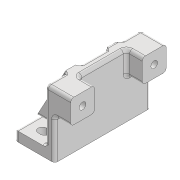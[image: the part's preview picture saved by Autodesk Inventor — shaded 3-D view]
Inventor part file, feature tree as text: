
AUTODESK INVENTOR PART (.ipt)
format: ipt  version: 2020 (Build 240168000, 168)  size: 386,048 bytes
history: native  units: mm
features: extrude x8, sketch x8, chamfer x2, other x1, fillet x1
ambient origin geometry x8: Origin, YZ Plane, XZ Plane, XY Plane, X Axis, Y Axis, Z Axis, Center Point
bodies: Body1 (feature_tree)
feature tree (20):
  other  "Sólido1"
  extrude  "Extrusão1"  Depth=40.0mm
  extrude  "Extrusão2"  Depth=6.0mm
  extrude  "Extrusão3"  Depth=6.0mm TaperAngle=0.0deg
  extrude  "Extrusão4"  TaperAngle=0.0deg  [1 undecoded]
  extrude  "Extrusão5"  Depth=15.0mm
  extrude  "Extrusão6"  Depth=4.2mm
  extrude  "Extrusão7"  Depth=10.0mm TaperAngle=0.0deg
  chamfer  "Chanfro2"  Distance=7.5mm
  chamfer  "Chanfro3"  Distance=7.5mm
  fillet  "Arredondamento1"  Radius=7.5mm
  extrude  "Extrusão8"  Depth=2.0mm TaperAngle=0.0deg
  sketch  "Esboço1"  dims[d0=25.0mm d1=40.0mm]
  sketch  "Esboço2"  dims[d2=60.0mm d3=0.0mm d4=6.0mm]
  sketch  "Esboço3"  dims[d5=6.0mm d6=40.0mm d7=0.0mm]
  sketch  "Esboço4"  dims[d8=15.0mm d9=0.0mm]
  sketch  "Esboço5"  dims[d10=0.0mm d11=15.0mm]
  sketch  "Esboço6"  dims[d12=15.0mm d13=4.2mm]
  sketch  "Esboço7"  dims[d14=4.2mm d15=10.0mm d16=0.0mm]
  sketch  "Esboço8"  dims[d17=7.5mm d18=7.5mm d19=7.5mm d20=7.5mm d21=50.0mm d22=0.0mm d23=6.9mm d24=6.9mm d25=6.0mm d26=0.0mm d27=5.3mm d28=5.3mm d29=8.0mm d30=8.0mm d31=10.0mm d32=0.0mm d33=6.0mm d34=6.0mm d35=14.0mm d36=14.0mm d37=19.0mm d38=0.0mm d42=33.0mm d43=18.0mm d44=45.0deg d45=33.0mm d46=18.0mm d47=45.0deg d48=2.0mm d49=1.5mm d50=1.5mm d51=19.0mm d52=0.0mm]
note: 1 required parameter value undecoded (feature->parameter linkage not recoverable at this tier; creation-order binding heuristic only, values carry confidence <= 0.55)
